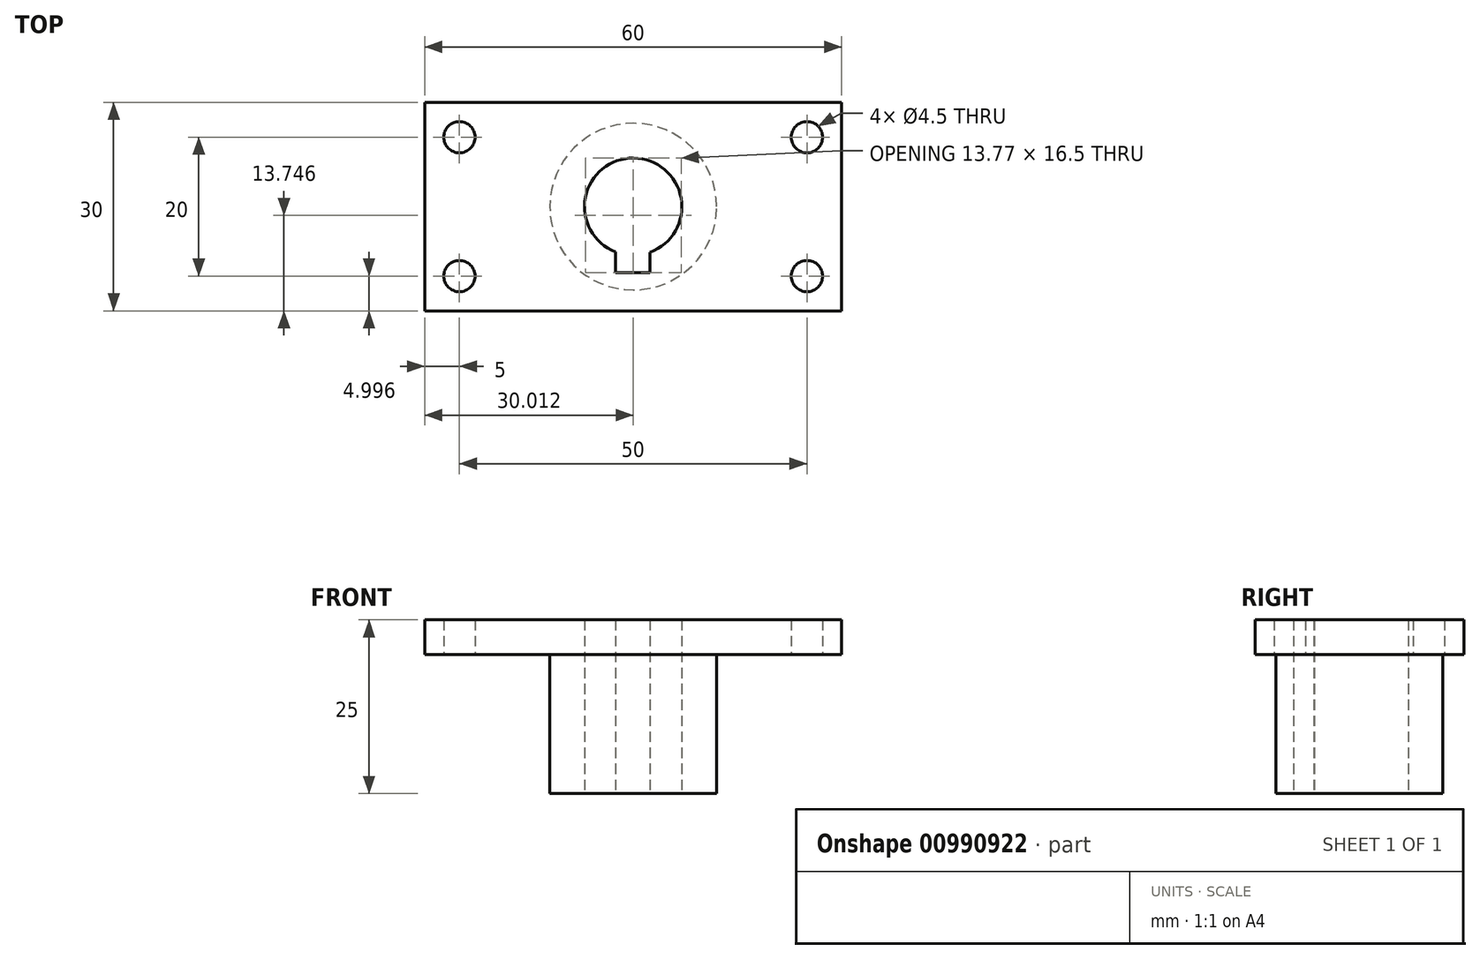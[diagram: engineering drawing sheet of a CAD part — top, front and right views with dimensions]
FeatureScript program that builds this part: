
annotation { "Feature Type Name" : "Feature", "Feature Type Description" : "" }
export const myFeature = defineFeature(function(context is Context, id is Id, definition is map)
    precondition{}
    {
        {
            var Q0;
            Q0=qCreatedBy(makeId("Top.planeOp"),FACE);
            var sketch = newSketch(context, id + "F0", { "sketchPlane" : qUnion([Q0])});
            skLineSegment(sketch, "E0.bottom", {"start": v(30, -14.82) * mm, "end": v(-30, -14.82) * mm});
            skLineSegment(sketch, "E0.top", {"start": v(30, 15.18) * mm, "end": v(-30, 15.18) * mm});
            skLineSegment(sketch, "E0.left", {"start": v(30, -14.82) * mm, "end": v(30, 15.18) * mm});
            skLineSegment(sketch, "E0.right", {"start": v(-30, -14.82) * mm, "end": v(-30, 15.18) * mm});
            skArc(sketch, "E1", {"start": v(2.44, -6.39) * mm, "mid": v(0.07, 7.18) * mm, "end": v(-2.56, -6.34) * mm});
            skCircle(sketch, "E2", {"center": v(0, 0.18) * mm, "radius": 12 * mm});
            skLineSegment(sketch, "E3", {"start": v(-30, 10.18) * mm, "end": v(30, 10.18) * mm, "construction": true});
            skLineSegment(sketch, "E4", {"start": v(-30, -9.82) * mm, "end": v(30, -9.82) * mm, "construction": true});
            skLineSegment(sketch, "E5", {"start": v(-25, -14.82) * mm, "end": v(-25, 15.18) * mm, "construction": true});
            skLineSegment(sketch, "E6", {"start": v(25, 15.18) * mm, "end": v(25, -14.82) * mm, "construction": true});
            skLineSegment(sketch, "E7", {"start": v(0, 15.18) * mm, "end": v(0, -14.82) * mm, "construction": true});
            skLineSegment(sketch, "E8", {"start": v(-2.56, -6.34) * mm, "end": v(-2.56, -9.32) * mm});
            skLineSegment(sketch, "E9", {"start": v(-2.56, -9.32) * mm, "end": v(2.44, -9.32) * mm});
            skLineSegment(sketch, "E10", {"start": v(2.44, -9.32) * mm, "end": v(2.44, -6.39) * mm});
            skPoint(sketch, "E11", {"position": v(0, -6.82) * mm});
            skCircle(sketch, "E12", {"center": v(-25, 10.18) * mm, "radius": 2 * mm});
            skCircle(sketch, "E13", {"center": v(25, 10.18) * mm, "radius": 2 * mm});
            skCircle(sketch, "E14", {"center": v(-25, -9.82) * mm, "radius": 2 * mm});
            skCircle(sketch, "E15", {"center": v(25, -9.82) * mm, "radius": 2 * mm});
            skCircle(sketch, "E16", {"center": v(0, 0) * mm, "radius": 2.5 * mm});
            skSolve(sketch);
        }
        {
            var Q0;
            Q0=makeQuery(id+"F0.imprint","IMPRINT",FACE,{"disambiguationData":[TD([[makeQuery(id+"F0.imprint","IMPRINT",EDGE,{"derivedFrom":sQuery(id+"F0.wireOp",EDGE,"E0.bottom")}),-1.0]])]});
            var Q1;
            Q1=makeQuery(id+"F0.imprint","IMPRINT",FACE,{"disambiguationData":[TD([[makeQuery(id+"F0.imprint","IMPRINT",EDGE,{"derivedFrom":sQuery(id+"F0.wireOp",EDGE,"E1")}),-1.0]])]});
            extrude(context, id + "F1", {"entities" : qUnion([Q0, Q1]), "depth" : 25 * mm, "offsetDistance" : 25 * mm});
        }
        {
            var Q0;
            Q0=sQuery(id+"F0.wireOp",VERTEX,"E14.center");
            var Q1;
            Q1=sQuery(id+"F0.wireOp",VERTEX,"E12.center");
            var Q2;
            Q2=sQuery(id+"F0.wireOp",VERTEX,"E13.center");
            var Q3;
            Q3=sQuery(id+"F0.wireOp",VERTEX,"E15.center");
            var Q4;
            Q4=makeQuery(id+"F1.opExtrude","SWEPT_BODY",BODY,{"disambiguationData":[OSD([sQuery(id+"F0.wireOp",EDGE,"E0.bottom"),sQuery(id+"F0.wireOp",EDGE,"E0.top"),sQuery(id+"F0.wireOp",EDGE,"E0.left"),sQuery(id+"F0.wireOp",EDGE,"E0.right"),sQuery(id+"F0.wireOp",EDGE,"E1"),sQuery(id+"F0.wireOp",EDGE,"E8"),sQuery(id+"F0.wireOp",EDGE,"E9"),sQuery(id+"F0.wireOp",EDGE,"E10"),sQuery(id+"F0.wireOp",EDGE,"E12"),sQuery(id+"F0.wireOp",EDGE,"E13"),sQuery(id+"F0.wireOp",EDGE,"E14"),sQuery(id+"F0.wireOp",EDGE,"E15")])]});
            hole(context, id + "F2", {"style" : HoleStyle.SIMPLE, "endStyle" : HoleEndStyle.THROUGH, "oppositeDirection" : true, "standardTappedOrClearance" : lookupTablePath({ "fit" : "Normal", "standard" : "ISO", "size" : "M4", "type" : "Clearance" }), "standardBlindInLast" : lookupTablePath({ "fit" : "Normal", "standard" : "ISO", "engagement" : "75%", "pitch" : "0.7 mm", "size" : "M4", "type" : "Clearance & tapped" }), "holeDiameter" : 4.5 * mm, "majorDiameter" : 5 * mm, "isTappedThrough" : true, "tappedDepth" : 12 * mm, "tapClearance" : 3, "locations" : qUnion([Q0, Q1, Q2, Q3]), "scope" : qUnion([Q4])});
        }
        {
            var Q0;
            Q0=makeQuery(id+"F0.imprint","IMPRINT",FACE,{"disambiguationData":[TD([[makeQuery(id+"F0.imprint","IMPRINT",EDGE,{"derivedFrom":sQuery(id+"F0.wireOp",EDGE,"E0.bottom")}),-1.0]])]});
            extrude(context, id + "F3", {"entities" : qUnion([Q0]), "operationType" : NewBodyOperationType.REMOVE, "depth" : 20 * mm, "offsetDistance" : 25 * mm});
        }
    });
